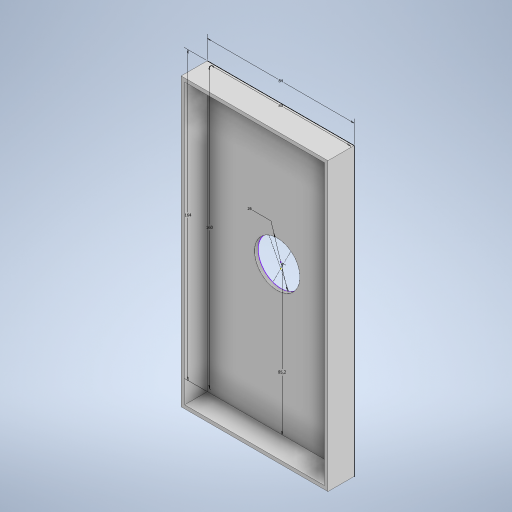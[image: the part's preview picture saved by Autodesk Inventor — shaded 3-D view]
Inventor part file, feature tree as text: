
AUTODESK INVENTOR PART (.ipt)
format: ipt  version: 2023 (Build 270158000, 158)  size: 248,320 bytes
history: native  units: mm
features: extrude x2, sketch x1
ambient origin geometry x8: Origin, YZ Plane, XZ Plane, XY Plane, X Axis, Y Axis, Z Axis, Center Point
bodies: Solid1 (feature_tree)
feature tree (3):
  sketch  "Sketch1"  dims[d0=80.0mm d1=160.0mm d2=84.0mm d3=164.0mm d4=26.0mm d5=85.2mm d6=2.0mm d7=0.0mm d8=15.0mm d9=0.0mm]
  extrude  "Extrusion1"  Depth=160.0mm
  extrude  "Extrusion2"  Depth=84.0mm
